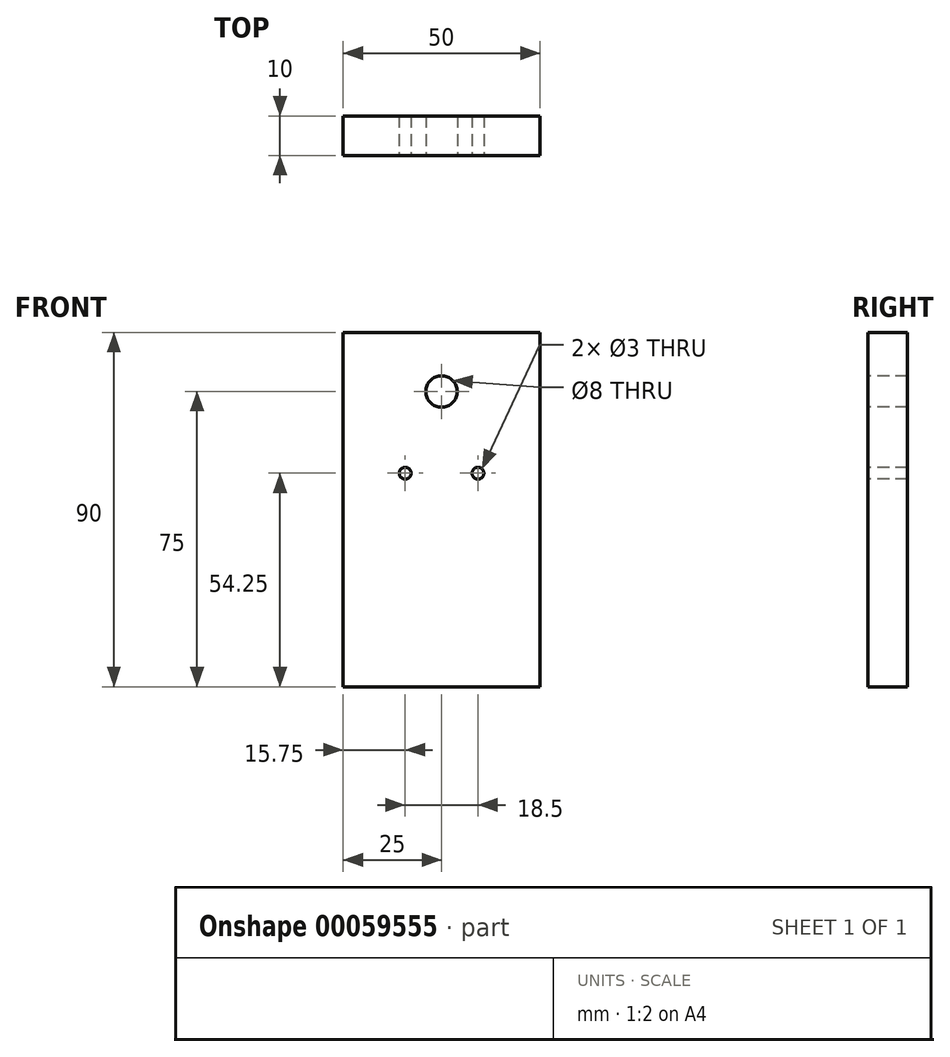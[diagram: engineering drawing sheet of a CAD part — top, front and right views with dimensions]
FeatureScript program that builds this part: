
annotation { "Feature Type Name" : "Feature", "Feature Type Description" : "" }
export const myFeature = defineFeature(function(context is Context, id is Id, definition is map)
    precondition{}
    {
        {
            var Q0;
            Q0=qCreatedBy(makeId("Front.planeOp"),FACE);
            var sketch = newSketch(context, id + "F0", { "sketchPlane" : qUnion([Q0])});
            skLineSegment(sketch, "E0.bottom", {"start": v(-25, 45) * mm, "end": v(25, 45) * mm});
            skLineSegment(sketch, "E0.top", {"start": v(-25, -45) * mm, "end": v(25, -45) * mm});
            skLineSegment(sketch, "E0.left", {"start": v(-25, 45) * mm, "end": v(-25, -45) * mm});
            skLineSegment(sketch, "E0.right", {"start": v(25, 45) * mm, "end": v(25, -45) * mm});
            skPoint(sketch, "E0.middle", {"position": v(0, 0) * mm});
            skSolve(sketch);
        }
        {
            var Q0;
            Q0 = qSketchRegion(id + "F0", true);
            extrude(context, id + "F1", {"entities" : qUnion([Q0]), "depth" : 10 * mm});
        }
        {
            var Q0;
            Q0=makeQuery(id+"F1.opExtrude","CAP_FACE",FACE,{"disambiguationData":[OSD([sQuery(id+"F0.wireOp",EDGE,"E0.bottom"),sQuery(id+"F0.wireOp",EDGE,"E0.top"),sQuery(id+"F0.wireOp",EDGE,"E0.left"),sQuery(id+"F0.wireOp",EDGE,"E0.right")])],"isStart":false});
            var sketch = newSketch(context, id + "F2", { "sketchPlane" : qUnion([Q0])});
            skCircle(sketch, "E1", {"center": v(0, 30) * mm, "radius": 4 * mm});
            skCircle(sketch, "E2", {"center": v(9.25, 9.25) * mm, "radius": 1.5 * mm});
            skCircle(sketch, "E3.MirrorC", {"center": v(-9.25, 9.25) * mm, "radius": 1.5 * mm});
            skSolve(sketch);
        }
        {
            var Q0;
            Q0 = qSketchRegion(id + "F2", true);
            extrude(context, id + "F3", {"entities" : qUnion([Q0]), "operationType" : NewBodyOperationType.REMOVE, "oppositeDirection" : true, "depth" : 25 * mm});
        }
    });
